# Revit family: Legrand_Enveloppes_industrielles_Metal_Armoires_Atlantic_Porte_vitree
name_source: partatom
category: Equipement électrique
revit_build: Autodesk Revit 2018 (Build: 20170223_1515(x64)
units: mm (PartAtom-declared; Revit-internal decimal feet)

## family parameters
Basée sur le plan de construction = Non
Configuration du panneau = Deux colonnes, circuits au sein
Cote de connecteur circulaire = Utiliser le diamètre
Couper avec des vides une fois chargée = Non
Numéro OmniClass = 23.80.30.11.17
Partagée = Non
Point de calcul de pièce = Non
Titre OmniClass = Distribution Boards and Control Panels
Toujours verticalement = Oui
Type d'élément = Tableau de raccordement

## types (6) — shared parameters
Conditions Générale d'Utilisation = https://export.legrand.com
ETIM Class 6.0 = EC000058
Fabricant = Legrand
IK = 10
IP = 66
Image du type = atlantic_porte_vitree_035495_pw_234023_pz_5.jpg
Matière = Polyester
RAL = 7035
URL = www.legrand.fr

## per-type parameters (varying)
| type | Coffret 035492 | Coffret 035493 | Coffret 035494 | Coffret 035495 | Coffret 035496 | Coffret 035497 | Description | Hauteur | Largeur | Poids | distance avant zone d'installation | distance coté zone d'installation | largeur zone d'installation | profondeur | profondeur zone d'installation |
| Legrand_Enveloppes_industrielles_Metal_Armoires_Atlantic_Porte_vitree 035492 | Oui | Non | Non | Non | Non | Non | Ref 035492 - Legrand_Enveloppes_industrielles_Metal_Armoires_Atlantic_Porte_vitree | 400 mm  [stored 1.31234 ft] | 300 mm | 6.00 kg | 300 mm | 200 mm  [stored 0.656168 ft] | 700 mm  [stored 2.29659 ft] | 200 mm  [stored 0.656168 ft] | 500 mm  [stored 1.64042 ft] |
| Legrand_Enveloppes_industrielles_Metal_Armoires_Atlantic_Porte_vitree 035493 | Non | Oui | Non | Non | Non | Non | Ref 035493 - Legrand_Enveloppes_industrielles_Metal_Armoires_Atlantic_Porte_vitree | 500 mm  [stored 1.64042 ft] | 400 mm  [stored 1.31234 ft] | 8.00 kg | 400 mm  [stored 1.31234 ft] | 200 mm  [stored 0.656168 ft] | 800 mm  [stored 2.62467 ft] | 200 mm  [stored 0.656168 ft] | 600 mm |
| Legrand_Enveloppes_industrielles_Metal_Armoires_Atlantic_Porte_vitree 035494 | Non | Non | Oui | Non | Non | Non | Ref 035494 - Legrand_Enveloppes_industrielles_Metal_Armoires_Atlantic_Porte_vitree | 600 mm | 400 mm  [stored 1.31234 ft] | 10.00 kg | 400 mm  [stored 1.31234 ft] | 250 mm  [stored 0.82021 ft] | 900 mm  [stored 2.95276 ft] | 250 mm  [stored 0.82021 ft] | 650 mm  [stored 2.13255 ft] |
| Legrand_Enveloppes_industrielles_Metal_Armoires_Atlantic_Porte_vitree 035495 | Non | Non | Non | Oui | Non | Non | Ref 035495 - Legrand_Enveloppes_industrielles_Metal_Armoires_Atlantic_Porte_vitree | 700 mm  [stored 2.29659 ft] | 500 mm  [stored 1.64042 ft] | 15.00 kg | 500 mm  [stored 1.64042 ft] | 250 mm  [stored 0.82021 ft] | 1000 mm  [stored 3.28084 ft] | 250 mm  [stored 0.82021 ft] | 750 mm  [stored 2.46063 ft] |
| Legrand_Enveloppes_industrielles_Metal_Armoires_Atlantic_Porte_vitree 035496 | Non | Non | Non | Non | Oui | Non | Ref 035496 - Legrand_Enveloppes_industrielles_Metal_Armoires_Atlantic_Porte_vitree | 800 mm  [stored 2.62467 ft] | 600 mm | 25.00 kg | 600 mm | 300 mm | 1200 mm | 300 mm | 900 mm  [stored 2.95276 ft] |
| Legrand_Enveloppes_industrielles_Metal_Armoires_Atlantic_Porte_vitree 035497 | Non | Non | Non | Non | Non | Oui | Ref 035497 - Legrand_Enveloppes_industrielles_Metal_Armoires_Atlantic_Porte_vitree | 1000 mm  [stored 3.28084 ft] | 800 mm  [stored 2.62467 ft] | 36.00 kg | 800 mm  [stored 2.62467 ft] | 300 mm | 1400 mm  [stored 4.59318 ft] | 300 mm | 1100 mm |

note: [stored X ft] marks values corroborated as IEEE doubles in the binary element streams (Revit-internal decimal feet)
